# Revit family: CP612.6T (Family)
name_source: partatom
category: Parking
units: mm (PartAtom-declared; Revit-internal decimal feet)

## family parameters
Always vertical = Yes
Cut with Voids When Loaded = No
Shared = No
Work Plane-Based = No

## types (6) — shared parameters
Column Upper Bottom = 373 mm
Upper Column Height = 1500 mm  [stored 4.92126 ft]

## per-type parameters (varying)
| type | Column Ht (A) | Model Height (DH) | Parking Width (PW) | Total Height (H) |
| 2000 x 2300 | 3000 mm | 1600 mm  [stored 5.24934 ft] | 2000 mm  [stored 6.56168 ft] | 3200 mm  [stored 10.4987 ft] |
| 2100 x 2400 | 3100 mm | 1700 mm  [stored 5.57743 ft] | 2100 mm | 3300 mm |
| 2200 x 2500 | 3200 mm  [stored 10.4987 ft] | 1800 mm | 2200 mm | 3400 mm |
| 2300 x 2600 | 3500 mm | 1900 mm | 2300 mm | 3500 mm |
| 2400 x 2700 | 3600 mm  [stored 11.811 ft] | 2000 mm  [stored 6.56168 ft] | 2400 mm  [stored 7.87402 ft] | 3600 mm  [stored 11.811 ft] |
| 2500 x 2800 | 3135 mm  [stored 10.2854 ft] | 1600 mm  [stored 5.24934 ft] | 2400 mm  [stored 7.87402 ft] | 3200 mm  [stored 10.4987 ft] |

note: [stored X ft] marks values corroborated as IEEE doubles in the binary element streams (Revit-internal decimal feet)

## geometry (parser evidence)
native form markers: Sweep x9
no freeform markers — native parametric forms only
